# Revit family: RootSpace® - Rev A
name_source: partatom
category: Site
units: mm (PartAtom-declared; Revit-internal decimal feet)

## family parameters
Always vertical = Yes
Cut with Voids When Loaded = No
Part Type = Normal
Round Connector Dimension = Use Diameter
Shared = No
Work Plane-Based = No

## types (5) — shared parameters
AssetType = Fixed
Color = Black
DurationUnit = year
ExpectedLife = 25
Finish = Natural
IfcExportAs = IfcBuildingElementProxyType
IfcExportType = NOTDEFINED
InstallationDate (default) = 1900-12-31T23:59:59
LoadBearing = Yes
ManufacturerName = GreenBlue Urban Ltd
ManufacturerURL = www.greenblue.com/gb
NBSDescription = Geocellular modular plastics structural soil units
NBSReference = 45-40-65/355
NBSVisibility-4 = No
Uniclass2015Code = Pr_45_63_63_62
Uniclass2015Version = Products v1.28
Version = 2
WarrantyDescription = www.greenblue.com/gb
WarrantyDurationUnit = year
zero-valued in all types: LoadBearingCapacity

## per-type parameters (varying)
| type | BIMObjectName | Category | Features | Material | ModelNumber | ModelReference | NBSCertification | NBSVisibility-1 | NBSVisibility-2 | NBSVisibility-3 | NBSVisibility-5 | Name | NominalHeight | NominalLength | NominalWidth | ProductInformation | Size | Uniclass2015Title | WarrantyStartDate | Weight |
| GBURAC600A | NBS_GreenBlueUrbanLtd_GeocellularModularPlasticsStructuralSoilUnits_Rootspace_600Upright | Pr_45_63_63_62:Plastics divided modular units | Arborsystem Compatible | Recycled Polypropylene | GBURAC600A | 600 Upright | www.nationalbimlibrary.com/cert/20zrwnqz | Yes | No | No | No | GeocellularModularPlasticsStructuralSoilUnits_Rootspace_600Upright_GreenBlueUrbanLtd | 600 mm | 500 mm  [stored 1.64042 ft] | 90 mm  [stored 0.295276 ft] | www.greenblue.com/gb/products/rootspace | 500 x 90 x 600 mm | Plastics divided modular units | 1900-12-31T23:59:59 | 1.930 kg |
| GBURAC400B | NBS_GreenBlueUrbanLtd_GeocellularModularPlasticsStructuralSoilUnits_RootSpace_400Upright | Pr_45_63_63_62:Plastics divided modular unit | Arborsystem Compatible | Recycled Polypropylene | GBURAC400B | 400 Upright |  | No | Yes | No | No | GeocellularModularPlasticsStructuralSoilUnits_RootSpace_400_GreenBlueUrbanLtd | 400 mm  [stored 1.31234 ft] | 500 mm  [stored 1.64042 ft] | 75 mm  [stored 0.246063 ft] | www.greenblue.com/gb/products/rootspace/ | 500 x 75 x 400 mm | Plastics divided modular unit | 1900-12-31T23:59:59 | 1.287 kg |
| GBURSP65A | NBS_GreenBlueUrbanLtd_GeocellularModularPlasticsStructuralSoilUnits_RootSpace_600Inﬁll | Pr_45_63_63_62:Plastics divided modular units |  | Recycled Polypropylene | GBURSP65A | 600 Infill | www.nationalbimlibrary.com/cert/shjxknda | No | No | Yes | No | GeocellularModularPlasticsStructuralSoilUnits_RootSpace_600Inﬁll_GreenBlueUrbanLtd | 585 mm  [stored 1.91929 ft] | 310 mm  [stored 1.01706 ft] | 40 mm  [stored 0.131234 ft] | www.greenblue.com/gb/products/rootspace | 310 x 40 x 585 mm | Plastics divided modular units | 1900-12-31T23-59-59 | 0.930 kg |
| GBUSP45PB | NBS_GreenBlueUrbanLtd_GeocellularModularPlasticsStructuralSoilUnits_RootSpace_400Inﬁll | Pr_45_63_63_62:Plastics divided modular units |  | Recycled Polypropylene | GBURSP45PB | 400 Infill |  | No | No | No | Yes | GeocellularModularPlasticsStructuralSoilUnits_RootSpace_400Inﬁll_GreenBlueUrbanLtd | 327 mm | 334 mm  [stored 1.0958 ft] | 40 mm  [stored 0.131234 ft] | www.greenblue.com/gb/products/rootspace | 334 x 40 x 327 mm | Plastics divided modular units | 1900-12-31T23:59:59 | 0.625 kg |
| GBURAC500A/B | NBS_GreenBlueUrbanLtd_GeocellularModularPlasticsStructuralSoilUnits_RootSpace_AirﬂowQRTop | Pr_45_63_63_62:Plastics divided modular units |  | Recyled Polypropylene | GBURAC500A/B | Airflow QR (Quick Release) Top | www.nationalbimlibrary.com/cert/dhhwt0ug | No | No | No | Yes | GeocellularModularPlasticsStructuralSoilUnits_RootSpace_AirﬂowQRTop_GreenBlueUrbanLtd | 75 mm  [stored 0.246063 ft] | 500 mm  [stored 1.64042 ft] | 500 mm  [stored 1.64042 ft] | www.greenblue.com/gb/products/rootspace | 500 x 500 x 75 mm | Plastics divided modular units | 1900-12-31T23:59:59 | 2.54 kg |

note: [stored X ft] marks values corroborated as IEEE doubles in the binary element streams (Revit-internal decimal feet)

## geometry (parser evidence)
native form markers: Sweep x25
no freeform markers — native parametric forms only
